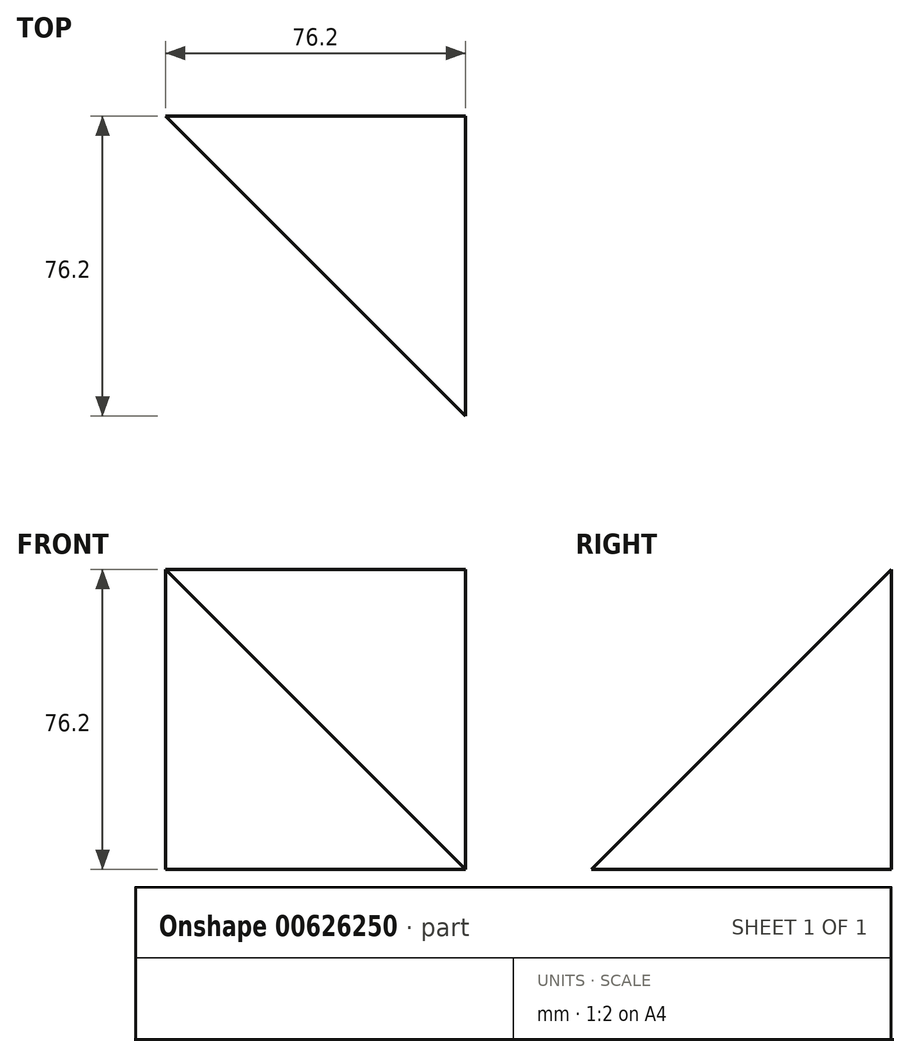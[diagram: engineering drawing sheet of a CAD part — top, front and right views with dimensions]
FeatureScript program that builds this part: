
annotation { "Feature Type Name" : "Feature", "Feature Type Description" : "" }
export const myFeature = defineFeature(function(context is Context, id is Id, definition is map)
    precondition{}
    {
        {
            var Q0;
            Q0=qCreatedBy(makeId("Right.planeOp"),FACE);
            var sketch = newSketch(context, id + "F0", { "sketchPlane" : qUnion([Q0])});
            skLineSegment(sketch, "E0.bottom", {"start": v(38.1, -38.1) * mm, "end": v(-38.1, -38.1) * mm});
            skLineSegment(sketch, "E0.top", {"start": v(38.1, 38.1) * mm, "end": v(-38.1, 38.1) * mm});
            skLineSegment(sketch, "E0.left", {"start": v(38.1, -38.1) * mm, "end": v(38.1, 38.1) * mm});
            skLineSegment(sketch, "E0.right", {"start": v(-38.1, -38.1) * mm, "end": v(-38.1, 38.1) * mm});
            skPoint(sketch, "E0.middle", {"position": v(0, 0) * mm});
            skSolve(sketch);
        }
        {
            var Q0;
            Q0 = qSketchRegion(id + "F0", true);
            extrude(context, id + "F1", {"entities" : qUnion([Q0]), "endBound" : BoundingType.SYMMETRIC, "depth" : 76.2 * mm, "offsetDistance" : 25.4 * mm});
        }
        {
            var Q0;
            Q0=makeQuery(id+"F1.opExtrude","CAP_FACE",FACE,{"disambiguationData":[OSD([sQuery(id+"F0.wireOp",EDGE,"E0.bottom"),sQuery(id+"F0.wireOp",EDGE,"E0.top"),sQuery(id+"F0.wireOp",EDGE,"E0.left"),sQuery(id+"F0.wireOp",EDGE,"E0.right")])],"isStart":false});
            var sketch = newSketch(context, id + "F2", { "sketchPlane" : qUnion([Q0])});
            skLineSegment(sketch, "E1", {"start": v(-38.1, 38.1) * mm, "end": v(38.1, 38.1) * mm});
            skLineSegment(sketch, "E2", {"start": v(38.1, 38.1) * mm, "end": v(-38.1, -38.1) * mm});
            skLineSegment(sketch, "E3", {"start": v(-38.1, -38.1) * mm, "end": v(-38.1, 38.1) * mm});
            skSolve(sketch);
        }
        {
            var Q0;
            Q0 = qSketchRegion(id + "F2", true);
            extrude(context, id + "F3", {"entities" : qUnion([Q0]), "operationType" : NewBodyOperationType.REMOVE, "oppositeDirection" : true, "depth" : 76.2 * mm, "offsetDistance" : 25.4 * mm});
        }
        {
            var Q0;
            Q0=makeQuery(id+"F1.opExtrude","SWEPT_FACE",FACE,{"disambiguationData":[OSD([sQuery(id+"F0.wireOp",EDGE,"E0.bottom")])]});
            var sketch = newSketch(context, id + "F4", { "sketchPlane" : qUnion([Q0])});
            skLineSegment(sketch, "E4", {"start": v(38.1, 38.1) * mm, "end": v(-38.1, -38.1) * mm});
            skLineSegment(sketch, "E5", {"start": v(-38.1, -38.1) * mm, "end": v(-38.1, 38.1) * mm});
            skLineSegment(sketch, "E6", {"start": v(-38.1, 38.1) * mm, "end": v(38.1, 38.1) * mm});
            skSolve(sketch);
        }
        {
            var Q0;
            Q0 = qSketchRegion(id + "F4", true);
            extrude(context, id + "F5", {"entities" : qUnion([Q0]), "operationType" : NewBodyOperationType.REMOVE, "oppositeDirection" : true, "depth" : 76.2 * mm, "offsetDistance" : 25.4 * mm});
        }
    });
